# Revit family: en-halla-gatu-recessedrfa
name_source: partatom
category: Осветительные приборы
revit_build: Autodesk Revit 2017 (Build: 20160225_1515(x64)
units: mm (PartAtom-declared; Revit-internal decimal feet)

## family parameters
Заголовок OmniClass = General Luminaries, Non Directional
Источник света = Нет
Номер OmniClass = 23.80.70.11.11
Общий = Нет
Основа = Грань
При загрузке вырезать с полостями = Нет
Размер круглого соединителя = Использовать диаметр
Тип детали = Нормальный
Точка расчета площади = Нет

## types (1)
- en-halla-gatu-recessedrfa
    Colour of luminaire = Sheet metal - white
    Date of publishing = 2014-12-13
    Depth = 0.00
    Design country = Czech Republic
    Distance X = 150 мм
    Distance Y = 75 мм
    Edition number = 2
    Electric potential = 12 В
    IFC Classification = Light Fixture
    LED source = Да
    Lighting height = 110 мм
    Lighting length = 330 мм
    Lighting width = 330 мм
    Manufacturer country = Czech Republic
    Manufacturer name = HALLA
    Material main = Sheet metal
    Material of luminaire = Plech
    NBS Reference Code = 49
    NBS Reference Description = Luminaires And Lamps
    Nominal height = 0.00
    Nominal width = 0.00
    Number of sources = 4
    Power input = 84 Вт
    Price (EUR) = 0 $
    Product SKU = gatu
    Product family = Indoor Luminaires
    Product group = GATU
    QR code = http://file-system.ru
    Source 1 = Нет
    Source 2 = Да
    Source 3 = Да
    UNSPSC Code = 3911
    URL = www.halla.cz
    Uniclass 1.4 Code = JY73
    Uniclass 1.4 Description = Luminaires and lamps
    Uniclass 2.0 Code = PR-49
    Uniclass 2.0 Description = Luminaires And Lamps
    Weight Net (Kg) = 0
    Изготовитель = HALLA
    Код по классификатору = D5020200
    Отметка по умолчанию = 2000 мм
    Полная установленная мощность = 84 В·А
